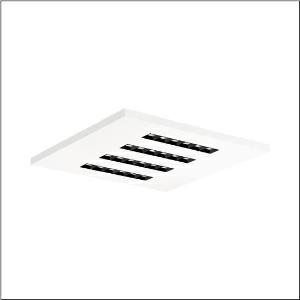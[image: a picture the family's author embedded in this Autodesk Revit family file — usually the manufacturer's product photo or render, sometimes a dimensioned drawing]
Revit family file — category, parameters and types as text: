
# Revit family: silica_21_square_51mx6kds44w
name_source: partatom
category: Lighting Fixtures
units: mm (PartAtom-declared; Revit-internal decimal feet)

## family parameters
Cut with Voids When Loaded = No
Host = Face
Light Source = No
Part Type = Normal
Room Calculation Point = No
Round Connector Dimension = Use Diameter
Shared = No

## types (1)
- --- (1 x LED, 4600 lm, 29.6 W, 4000K)
    Apparent Load = 30 VA
    CIE Flux Codes = 86 100 100 100 100
    Color Rendering = 80
    Color Temperature = 4000K
    Default Elevation = 1800 mm
    Description = Silica 21 Square, office luminaire, primary light control with lens, of PMMA, primary anti-glare with reflector, of PC, black, CAT 2 (L<= 3000cd/m²), light emission: direct distribution, primary light characteristic: symmetric, installation type: lay-in mounting, LED, rated luminous flux: 4.600lm, luminous efficacy: 155lm/W, light colour: 840, colour temperature: 4000K, control gear: DALI 2, with terminal, 5-pole, mains connection: 220..240V, AC, 50/60Hz, rated input power: 29.6W, luminaire housing, of sheet steel, coated, traffic white (RAL 9016), module: M600, length: 597mm, width: 597mm, height: 33mm, protection rating (complete): IP20, insulation class (complete): insulation class I (protective earthing), certification: CE, ENEC, VDE, permissible operating ambient temperature: -20..+40°C, standard: EN 50419, packaging unit: 1 piece
    Height = 0 mm  [stored 0 ft]
    Lamp = 1 x LED
    Lamp Light Flux = 4600 lm
    Lamp Power = 29.6 W
    Lamp count = 1
    Length = 597 mm
    Luminous efficacy = 155 lm/W
    Manufacturer = Siteco
    ModVariant = No
    Model = 51MX6KDS44W
    Mounting Place = Ceiling
    Mounting Type = Recessed
    Number of Poles = 1
    OnlyDefault = Yes
    Power Factor = 1
    Product Name = Silica 21 Square
    Product group = office luminaire | ceiling recessed
    ProductGroupID = 400
    Protection Class = Protection class I
    Protection Degree = IP 20
    RLX_Detail_Level = 1
    RLX_Emergency_Light_Flux = 0 lm
    RLX_Emergency_Type = 0
    RLX_Emergency_Type_DB = No
    RlxData = <blob elided: 21157 chars, md5=5eef66fe>
    Socket = socket
    Standby Power = 0 W
    System Light Flux = 4600 lm
    System Power = 30 W
    Type Comments = factory setting: luminous flux: 100 % | dim-lin: 254 | 399 mA
    Type Image = l_1275207.jpg
    URL = http://relux.com
    VarID = @adj_090635
    Voltage = 0 V
    Weight = 0.00 kg
    Width = 597 mm

note: [stored X ft] marks values corroborated as IEEE doubles in the binary element streams (Revit-internal decimal feet)

## geometry (parser evidence)
native form markers: Blend x4, Sweep x10
no freeform markers — native parametric forms only
